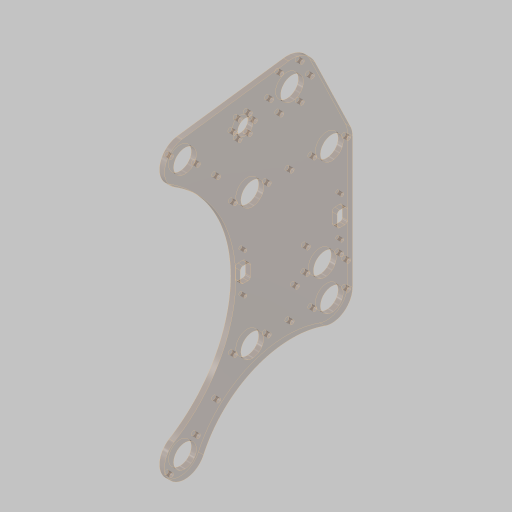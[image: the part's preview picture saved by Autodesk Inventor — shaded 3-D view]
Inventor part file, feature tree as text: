
AUTODESK INVENTOR PART (.ipt)
format: ipt  version: 2023.5 (Build 275446000, 446)  size: 520,192 bytes
history: native  units: in
note: dims shown in document units (in); Inventor stores cm internally (conversion verified against a paired STEP export)
features: sketch x7, hole x5, projected_geometry x3, extrude x2, fillet x1
ambient origin geometry x8: Origin, YZ Plane, XZ Plane, XY Plane, X Axis, Y Axis, Z Axis, Center Point
bodies: Solid1 (feature_tree)
feature tree (18):
  sketch  "Sketch1"  dims[d0=1.0in d1=2.0in]
  sketch  "Sketch2"  dims[d2=3.0in d4=3.8976in]
  extrude  "Extrusion1"  Depth=1.0in
  hole  "Hole1"  [1 undecoded]
  hole  "Hole2"  [1 undecoded]
  hole  "Hole3"  [1 undecoded]
  hole  "Hole4"  [1 undecoded]
  hole  "Hole5"  [1 undecoded]
  extrude  "Extrusion2"  Depth=0.13in
  fillet  "Fillet1"  Radius=1.115in
  sketch  "Sketch3"  dims[d5=3.6869in d6=12.0in]
  sketch  "Sketch4"  dims[d7=0.125in d8=0.125in]
  projected_geometry  "Projected Loop1"
  sketch  "Sketch5"  dims[d9=5.0in d10=15.0in]
  sketch  "Sketch6"  dims[d11=2.0in d12=2.0in]
  sketch  "Sketch7"  dims[d13=4.4882in d14=11.0in d15=1.115in d16=1.5in d17=3.095in d18=2.0in d19=0.25in d31=1.655in d32=0.375in d33=0.25in d34=0.0in d35=1.9488in d36=1.5in d37=1.0in d38=0.75in d50=0.5in d51=0.5in d52=0.201in d53=0.75in d54=0.385in d55=0.25in d56=0.5635in d57=1.0in d58=0.8108in d59=2.3622in d61=360.0deg d63=2.9551in d64=3.0in d68=4.25in d69=1.0in d70=3.0in d71=2.5in d72=3.2185in d73=6.4369in d74=4.7835in d75=1.7in d77=2.0in d78=2.3622in d80=360.0deg d82=0.201in d83=0.75in d84=0.385in d85=0.25in d86=0.5635in d87=1.0in d88=0.8108in d89=0.201in d90=0.328in d91=0.385in d92=0.25in d93=0.5635in d94=1.0in d95=0.8108in d97=1.5in d98=2.517in d99=2.517in d101=0.481in d102=1.25in d104=0.201in d105=0.75in d106=0.375in d107=0.25in d108=0.5635in d109=1.0in d110=0.8108in d111=0.375in d112=0.375in d113=0.375in d114=1.9366in d115=0.5in d116=1.9366in d117=4.75in d118=0.15in d119=0.75in d120=0.279in d121=0.25in d122=0.5635in d123=1.0in d124=0.8108in d125=0.5in d126=0.75in d127=1.0in d128=0.0in d129=0.13in]
  projected_geometry  "Project Cut Edges1"
  projected_geometry  "Project Cut Edges2"
note: 5 required parameter values undecoded (feature->parameter linkage not recoverable at this tier; creation-order binding heuristic only, values carry confidence <= 0.55)
